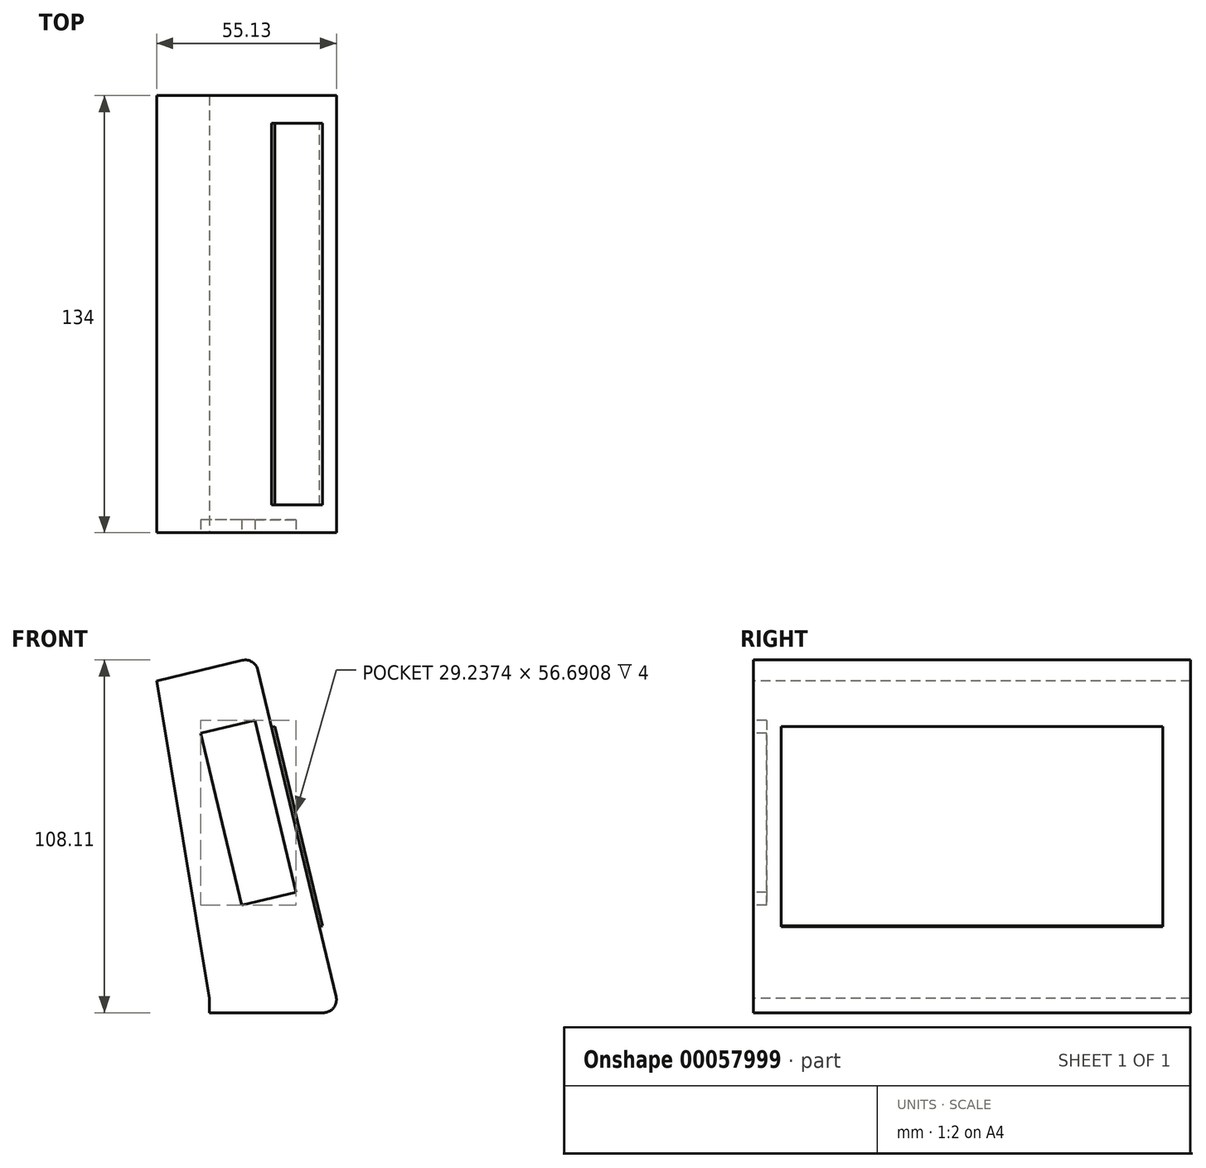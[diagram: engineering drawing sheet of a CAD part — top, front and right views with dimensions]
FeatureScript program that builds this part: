
annotation { "Feature Type Name" : "Feature", "Feature Type Description" : "" }
export const myFeature = defineFeature(function(context is Context, id is Id, definition is map)
    precondition{}
    {
        {
            var Q0;
            Q0=qCreatedBy(makeId("Front.planeOp"),FACE);
            var sketch = newSketch(context, id + "F0", { "sketchPlane" : qUnion([Q0])});
            skLineSegment(sketch, "E0", {"start": v(0, 0) * mm, "end": v(34.93, 0) * mm});
            skLineSegment(sketch, "E1", {"start": v(38.82, 4.93) * mm, "end": v(14.88, 105.04) * mm});
            skLineSegment(sketch, "E2", {"start": v(10.06, 108) * mm, "end": v(-16.2, 101.72) * mm});
            skLineSegment(sketch, "E3", {"start": v(-16.2, 101.72) * mm, "end": v(0, 0) * mm, "construction": true});
            skLineSegment(sketch, "E4", {"start": v(13.93, 89.65) * mm, "end": v(26.54, 36.93) * mm});
            skLineSegment(sketch, "E5", {"start": v(26.54, 36.93) * mm, "end": v(9.9, 32.96) * mm});
            skLineSegment(sketch, "E6", {"start": v(9.9, 32.96) * mm, "end": v(-2.7, 85.67) * mm});
            skLineSegment(sketch, "E7", {"start": v(13.93, 89.65) * mm, "end": v(-2.7, 85.67) * mm});
            skPoint(sketch, "E8.visualSharp", {"position": v(13.95, 108.93) * mm});
            skArc(sketch, "E8.filletArc", {"start": v(14.88, 105.04) * mm, "mid": v(13.08, 107.52) * mm, "end": v(10.06, 108) * mm});
            skPoint(sketch, "E9.visualSharp", {"position": v(40, 0) * mm});
            skArc(sketch, "E9.filletArc", {"start": v(34.93, 0) * mm, "mid": v(38.07, 1.52) * mm, "end": v(38.82, 4.93) * mm});
            skLineSegment(sketch, "E10", {"start": v(0, 0) * mm, "end": v(0, 4.45) * mm});
            skLineSegment(sketch, "E11", {"start": v(0, 4.45) * mm, "end": v(-16.2, 101.72) * mm});
            skSolve(sketch);
        }
        {
            var Q0;
            Q0=makeQuery(id+"F0.imprint","IMPRINT",FACE,{"disambiguationData":[TD([[makeQuery(id+"F0.imprint","IMPRINT",EDGE,{"derivedFrom":sQuery(id+"F0.wireOp",EDGE,"E0")}),1.0]])]});
            var Q1;
            Q1=makeQuery(id+"F0.imprint","IMPRINT",FACE,{"disambiguationData":[TD([[makeQuery(id+"F0.imprint","IMPRINT",EDGE,{"derivedFrom":sQuery(id+"F0.wireOp",EDGE,"E4")}),-1.0]])]});
            extrude(context, id + "F1", {"entities" : qUnion([Q0, Q1]), "oppositeDirection" : true, "depth" : 134 * mm});
        }
        {
            var Q0;
            Q0=makeQuery(id+"F0.imprint","IMPRINT",FACE,{"disambiguationData":[TD([[makeQuery(id+"F0.imprint","IMPRINT",EDGE,{"derivedFrom":sQuery(id+"F0.wireOp",EDGE,"E4")}),-1.0]])]});
            extrude(context, id + "F2", {"entities" : qUnion([Q0]), "operationType" : NewBodyOperationType.REMOVE, "oppositeDirection" : true, "depth" : 4 * mm});
        }
        {
            var Q0;
            Q0=makeQuery(id+"F1.opExtrude","SWEPT_FACE",FACE,{"disambiguationData":[OSD([sQuery(id+"F0.wireOp",EDGE,"E1")])]});
            var sketch = newSketch(context, id + "F3", { "sketchPlane" : qUnion([Q0])});
            skLineSegment(sketch, "E12.bottom", {"start": v(8.5, 80.7) * mm, "end": v(125.5, 80.7) * mm});
            skLineSegment(sketch, "E12.top", {"start": v(8.5, 17.77) * mm, "end": v(125.5, 17.77) * mm});
            skLineSegment(sketch, "E12.left", {"start": v(8.5, 80.7) * mm, "end": v(8.5, 17.77) * mm});
            skLineSegment(sketch, "E12.right", {"start": v(125.5, 80.7) * mm, "end": v(125.5, 17.77) * mm});
            skLineSegment(sketch, "E13", {"start": v(8.5, 80.7) * mm, "end": v(8.5, 98.7) * mm, "construction": true});
            skLineSegment(sketch, "E14", {"start": v(8.5, 80.7) * mm, "end": v(0, 80.7) * mm, "construction": true});
            skLineSegment(sketch, "E15", {"start": v(125.5, 17.77) * mm, "end": v(134, 17.77) * mm, "construction": true});
            skLineSegment(sketch, "E16", {"start": v(125.5, 17.77) * mm, "end": v(125.5, -4.23) * mm, "construction": true});
            skSolve(sketch);
        }
        {
            var Q0;
            Q0=makeQuery(id+"F3.imprint","IMPRINT",FACE,{"disambiguationData":[TD([[makeQuery(id+"F3.imprint","IMPRINT",EDGE,{"derivedFrom":sQuery(id+"F3.wireOp",EDGE,"E12.bottom")}),-1.0]])]});
            extrude(context, id + "F4", {"entities" : qUnion([Q0]), "operationType" : NewBodyOperationType.ADD, "depth" : 1 * mm});
        }
    });
